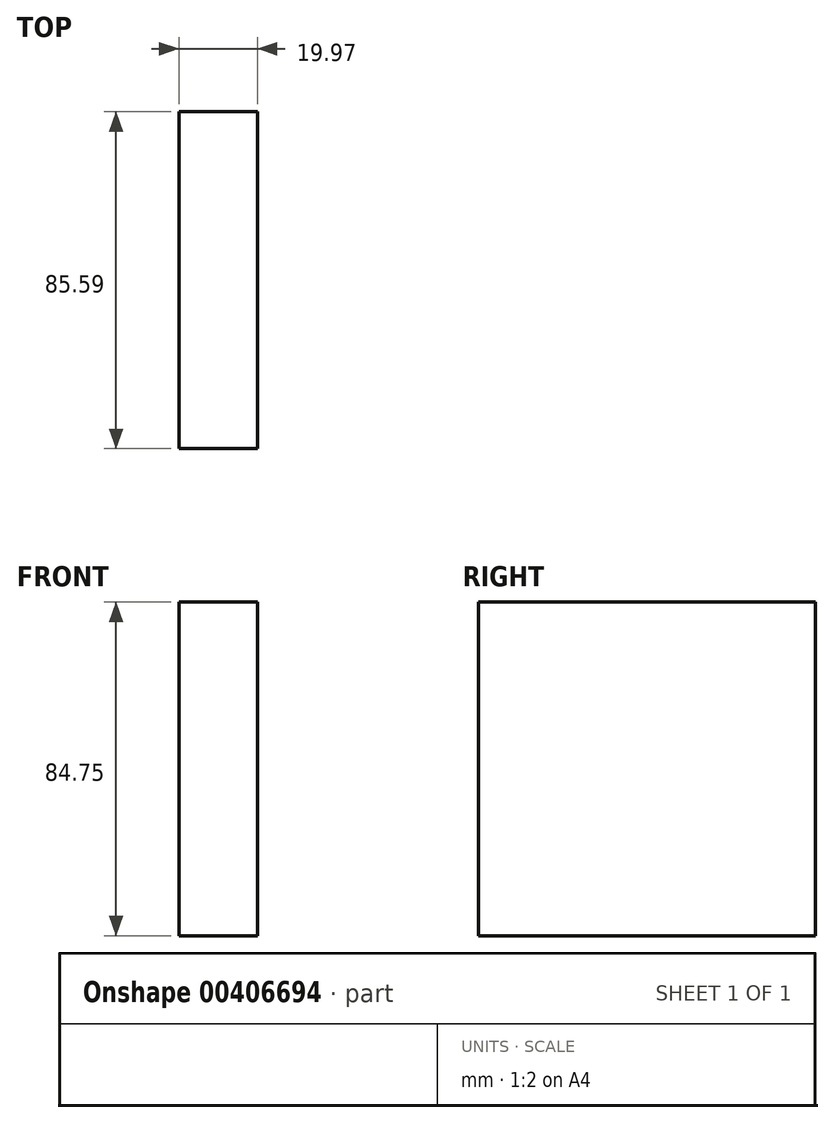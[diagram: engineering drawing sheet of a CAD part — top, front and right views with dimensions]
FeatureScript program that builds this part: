
annotation { "Feature Type Name" : "Feature", "Feature Type Description" : "" }
export const myFeature = defineFeature(function(context is Context, id is Id, definition is map)
    precondition{}
    {
        {
            var Q0;
            Q0=qCreatedBy(makeId("Right.planeOp"),FACE);
            var sketch = newSketch(context, id + "F0", { "sketchPlane" : qUnion([Q0])});
            skLineSegment(sketch, "E0.bottom", {"start": v(-41.55, 38.57) * mm, "end": v(44.04, 38.57) * mm});
            skLineSegment(sketch, "E0.top", {"start": v(-41.55, -46.18) * mm, "end": v(44.04, -46.18) * mm});
            skLineSegment(sketch, "E0.left", {"start": v(-41.55, 38.57) * mm, "end": v(-41.55, -46.18) * mm});
            skLineSegment(sketch, "E0.right", {"start": v(44.04, 38.57) * mm, "end": v(44.04, -46.18) * mm});
            skSolve(sketch);
        }
        {
            var Q0;
            Q0=makeQuery(id+"F0.imprint","IMPRINT",FACE,{"disambiguationData":[TD([[makeQuery(id+"F0.imprint","IMPRINT",EDGE,{"derivedFrom":sQuery(id+"F0.wireOp",EDGE,"E0.bottom")}),-1.0]])]});
            extrude(context, id + "F1", {"entities" : qUnion([Q0]), "oppositeDirection" : true, "depth" : 19.97 * mm});
        }
    });
